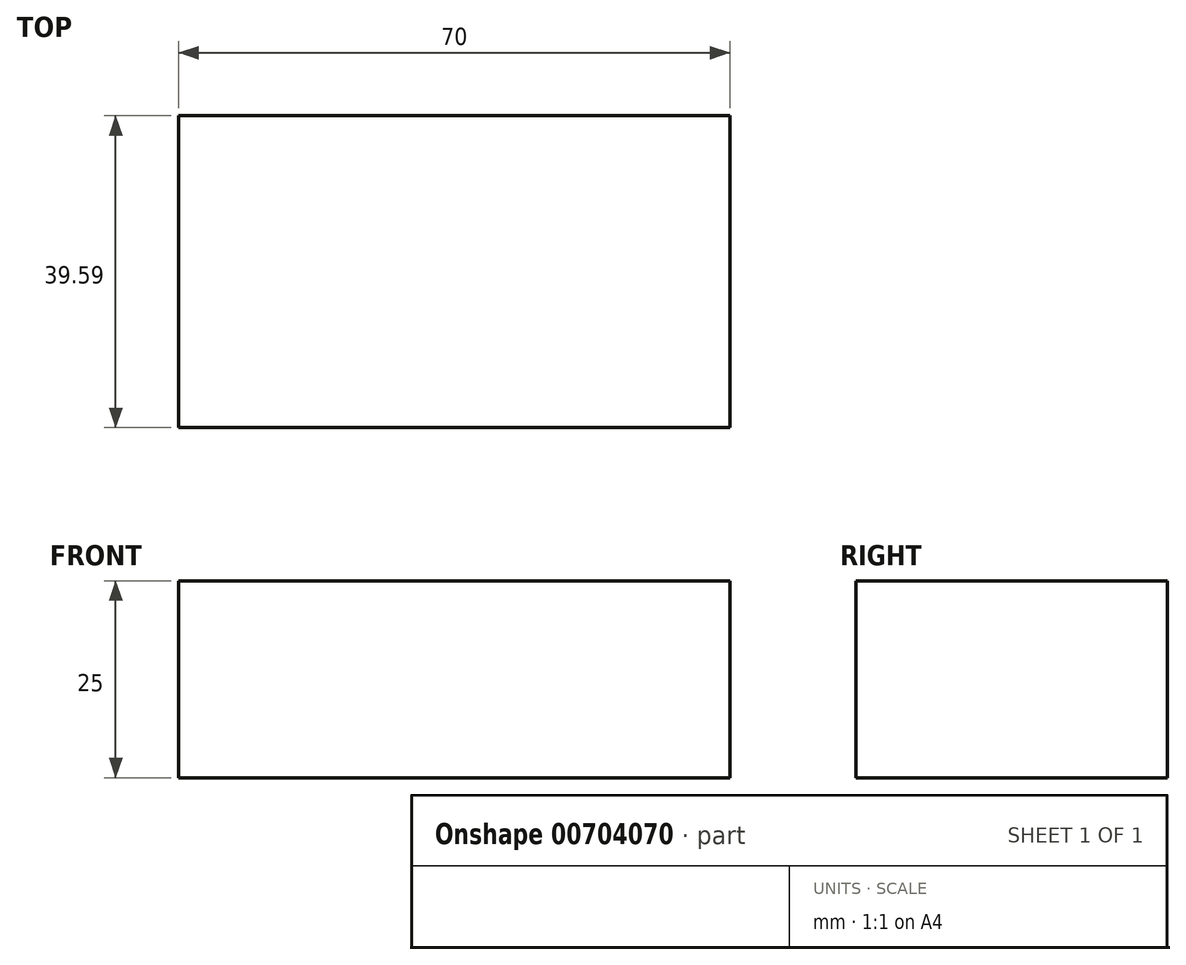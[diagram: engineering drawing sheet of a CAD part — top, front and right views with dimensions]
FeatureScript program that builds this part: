
annotation { "Feature Type Name" : "Feature", "Feature Type Description" : "" }
export const myFeature = defineFeature(function(context is Context, id is Id, definition is map)
    precondition{}
    {
        {
            var Q0;
            Q0=qCreatedBy(makeId("Top.planeOp"),FACE);
            var sketch = newSketch(context, id + "F0", { "sketchPlane" : qUnion([Q0])});
            skLineSegment(sketch, "E0.bottom", {"start": v(0, 0) * mm, "end": v(70, 0) * mm});
            skLineSegment(sketch, "E0.top", {"start": v(0, -39.6) * mm, "end": v(70, -39.6) * mm});
            skLineSegment(sketch, "E0.left", {"start": v(0, 0) * mm, "end": v(0, -39.6) * mm});
            skLineSegment(sketch, "E0.right", {"start": v(70, 0) * mm, "end": v(70, -39.6) * mm});
            skSolve(sketch);
        }
        {
            var Q0;
            Q0 = qSketchRegion(id + "F0", true);
            extrude(context, id + "F1", {"entities" : qUnion([Q0]), "depth" : 25 * mm, "offsetDistance" : 25 * mm});
        }
    });
